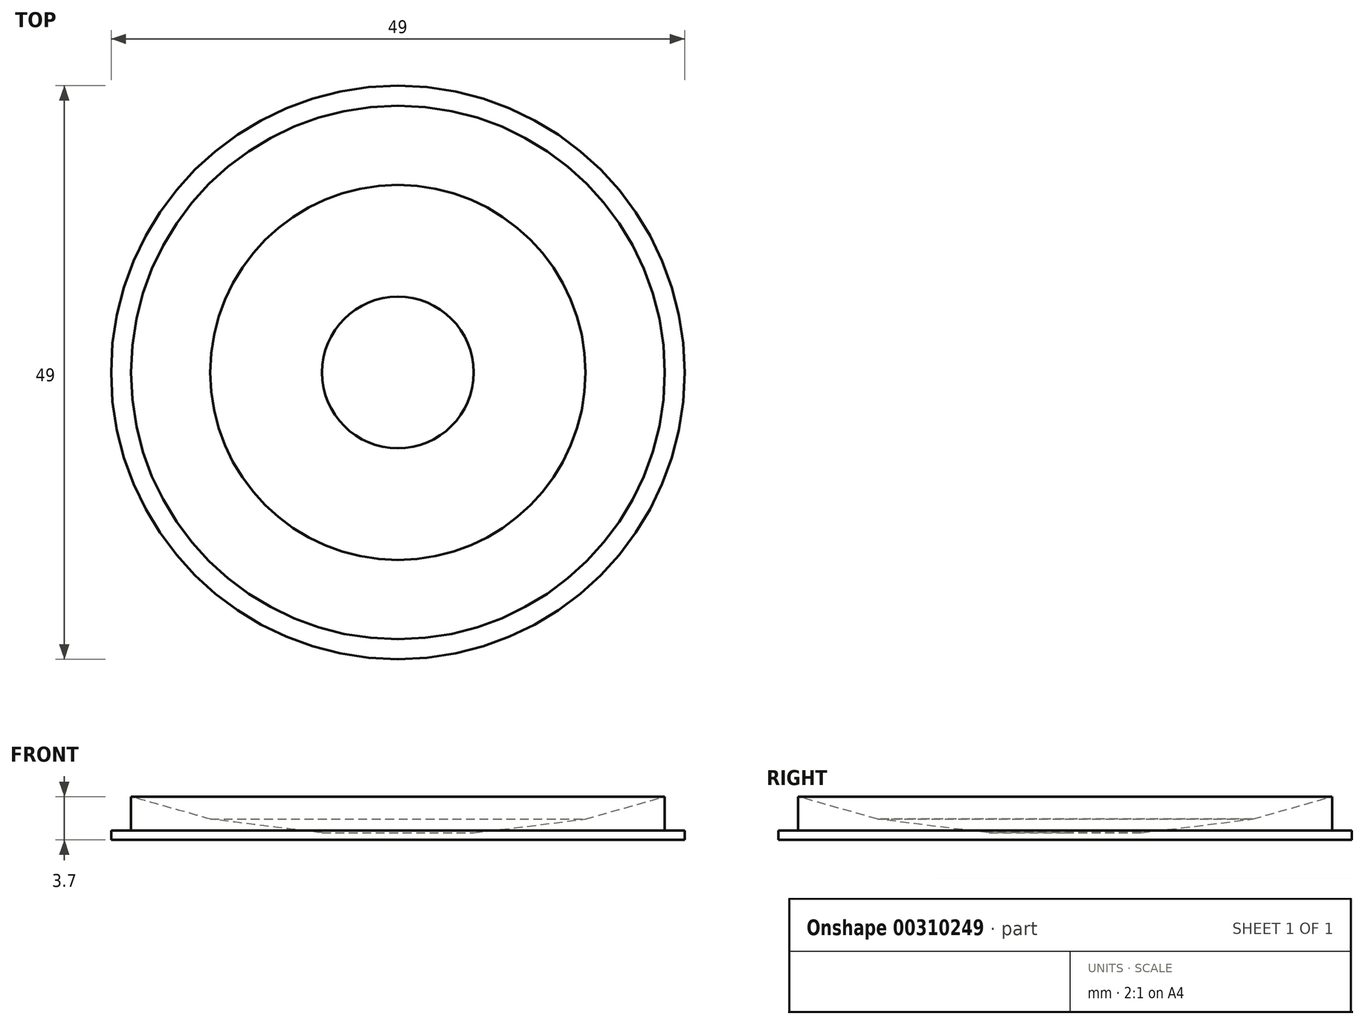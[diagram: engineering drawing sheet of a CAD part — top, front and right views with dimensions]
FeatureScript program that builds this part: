
annotation { "Feature Type Name" : "Feature", "Feature Type Description" : "" }
export const myFeature = defineFeature(function(context is Context, id is Id, definition is map)
    precondition{}
    {
        {
            var Q0;
            Q0=qCreatedBy(makeId("Front.planeOp"),FACE);
            var sketch = newSketch(context, id + "F0", { "sketchPlane" : qUnion([Q0])});
            skLineSegment(sketch, "E0", {"start": v(0, 0) * mm, "end": v(23, 0) * mm, "construction": true});
            skArc(sketch, "E1", {"start": v(0, -23) * mm, "mid": v(16.26, -16.26) * mm, "end": v(23, 0) * mm, "construction": true});
            skArc(sketch, "E2.0", {"start": v(0, -24.5) * mm, "mid": v(17.32, -17.32) * mm, "end": v(24.5, 0) * mm, "construction": true});
            skLineSegment(sketch, "E3", {"start": v(0, -23) * mm, "end": v(0, -24.5) * mm, "construction": true});
            skLineSegment(sketch, "E4", {"start": v(23, 0) * mm, "end": v(24.5, 0) * mm, "construction": true});
            skLineSegment(sketch, "E5", {"start": v(0, -23) * mm, "end": v(0, 0) * mm, "construction": true});
            skLineSegment(sketch, "E6", {"start": v(0, 0) * mm, "end": v(0, 48) * mm, "construction": true});
            skLineSegment(sketch, "E7", {"start": v(23, 0) * mm, "end": v(23, 48) * mm, "construction": true});
            skLineSegment(sketch, "E8", {"start": v(23, 48) * mm, "end": v(24.5, 48) * mm, "construction": true});
            skLineSegment(sketch, "E9", {"start": v(24.5, 48) * mm, "end": v(24.5, 0) * mm, "construction": true});
            skLineSegment(sketch, "E10", {"start": v(24.5, 0) * mm, "end": v(25.5, 0) * mm, "construction": true});
            skLineSegment(sketch, "E11", {"start": v(25.5, 0) * mm, "end": v(32.5, 0) * mm, "construction": true});
            skLineSegment(sketch, "E12", {"start": v(24.5, 43) * mm, "end": v(23, 43) * mm, "construction": true});
            skLineSegment(sketch, "E13", {"start": v(0, -24.5) * mm, "end": v(0, -25.5) * mm, "construction": true});
            skLineSegment(sketch, "E14", {"start": v(0, -25.5) * mm, "end": v(11.76, -20.92) * mm, "construction": true});
            skLineSegment(sketch, "E15", {"start": v(11.76, -20.92) * mm, "end": v(16.7, -17.92) * mm, "construction": true});
            skLineSegment(sketch, "E16", {"start": v(4.2, -22.61) * mm, "end": v(14.08, -18.19) * mm, "construction": true});
            skLineSegment(sketch, "E17", {"start": v(22.7, 40.5) * mm, "end": v(0, 40.5) * mm, "construction": true});
            skLineSegment(sketch, "E18", {"start": v(24.5, 44.5) * mm, "end": v(0, 44.5) * mm, "construction": true});
            skLineSegment(sketch, "E19", {"start": v(23, 48) * mm, "end": v(23, 44.7) * mm, "construction": true});
            skLineSegment(sketch, "E20", {"start": v(23, 44.7) * mm, "end": v(24.5, 44.7) * mm});
            skLineSegment(sketch, "E21", {"start": v(24.5, 44.7) * mm, "end": v(24.5, 44.2) * mm});
            skLineSegment(sketch, "E22", {"start": v(24.5, 44.2) * mm, "end": v(0, 44.2) * mm, "construction": true});
            skLineSegment(sketch, "E23", {"start": v(24.5, 44.2) * mm, "end": v(24.5, 43.4) * mm, "construction": true});
            skLineSegment(sketch, "E24", {"start": v(24.5, 43.4) * mm, "end": v(22.8, 43.4) * mm, "construction": true});
            skLineSegment(sketch, "E25", {"start": v(22.8, 43.4) * mm, "end": v(22.8, 40.5) * mm, "construction": true});
            skLineSegment(sketch, "E26", {"start": v(16.02, 42.42) * mm, "end": v(6.48, 43.6) * mm, "construction": true});
            skLineSegment(sketch, "E27", {"start": v(6.48, 43.6) * mm, "end": v(0, 43.6) * mm, "construction": true});
            skLineSegment(sketch, "E28", {"start": v(0, 44.2) * mm, "end": v(0, 43.6) * mm, "construction": true});
            skLineSegment(sketch, "E29", {"start": v(22.8, 40.5) * mm, "end": v(16.02, 42.42) * mm, "construction": true});
            skLineSegment(sketch, "E30.MirrorCS", {"start": v(24.5, 44.8) * mm, "end": v(0, 44.8) * mm});
            skLineSegment(sketch, "E31.MirrorCS", {"start": v(6.48, 45.4) * mm, "end": v(0, 45.4) * mm});
            skLineSegment(sketch, "E32.MirrorCS", {"start": v(16.02, 46.58) * mm, "end": v(6.48, 45.4) * mm});
            skLineSegment(sketch, "E33.MirrorCS", {"start": v(22.8, 48.5) * mm, "end": v(16.02, 46.58) * mm});
            skLineSegment(sketch, "E34.MirrorCS", {"start": v(22.8, 45.6) * mm, "end": v(22.8, 48.5) * mm});
            skLineSegment(sketch, "E35.MirrorCS", {"start": v(24.5, 45.6) * mm, "end": v(22.8, 45.6) * mm});
            skLineSegment(sketch, "E36", {"start": v(0, 45.4) * mm, "end": v(0, 44.8) * mm});
            skLineSegment(sketch, "E37", {"start": v(24.5, 45.6) * mm, "end": v(24.5, 44.8) * mm});
            skSolve(sketch);
        }
        {
            var Q0;
            Q0 = qSketchRegion(id + "F0", true);
            var Q1;
            Q1=sQuery(id+"F0.wireOp",EDGE,"E6");
            revolve(context, id + "F1", {"entities" : qUnion([Q0]), "axis" : qUnion([Q1]), "revolveType" : RevolveType.FULL});
        }
    });
